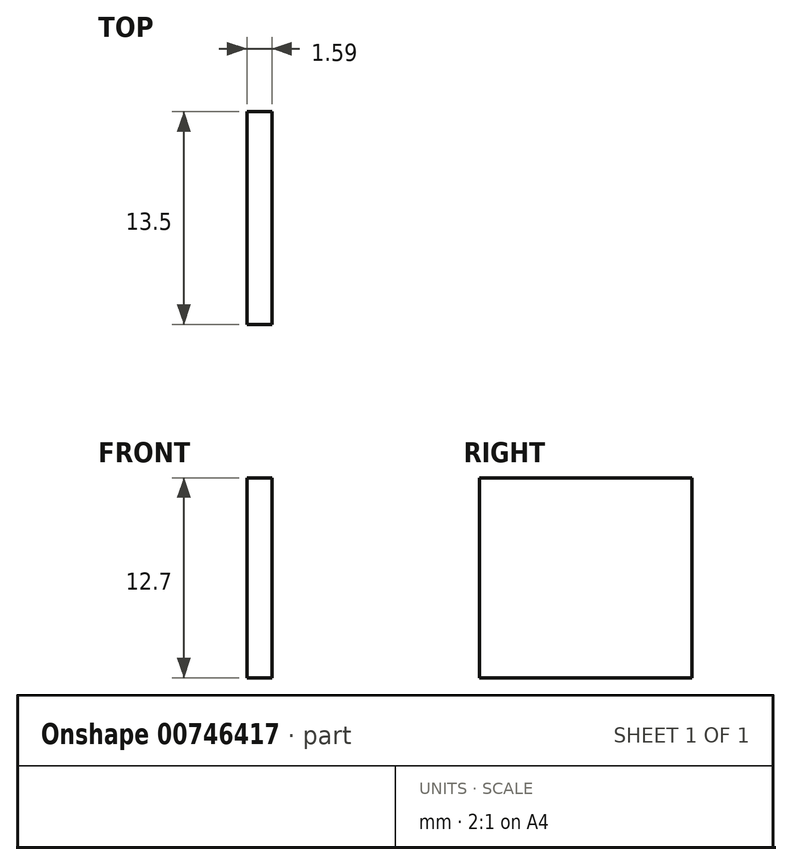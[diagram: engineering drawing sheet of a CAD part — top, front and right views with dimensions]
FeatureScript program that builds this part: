
annotation { "Feature Type Name" : "Feature", "Feature Type Description" : "" }
export const myFeature = defineFeature(function(context is Context, id is Id, definition is map)
    precondition{}
    {
        {
            var Q0;
            Q0=qCreatedBy(makeId("Right.planeOp"),FACE);
            var sketch = newSketch(context, id + "F0", { "sketchPlane" : qUnion([Q0])});
            skLineSegment(sketch, "E0.bottom", {"start": v(-6.75, 6.35) * mm, "end": v(6.75, 6.35) * mm});
            skLineSegment(sketch, "E0.top", {"start": v(-6.75, -6.35) * mm, "end": v(6.75, -6.35) * mm});
            skLineSegment(sketch, "E0.left", {"start": v(-6.75, 6.35) * mm, "end": v(-6.75, -6.35) * mm});
            skLineSegment(sketch, "E0.right", {"start": v(6.75, 6.35) * mm, "end": v(6.75, -6.35) * mm});
            skPoint(sketch, "E0.middle", {"position": v(0, 0) * mm});
            skSolve(sketch);
        }
        {
            var Q0;
            Q0 = qSketchRegion(id + "F0", true);
            extrude(context, id + "F1", {"entities" : qUnion([Q0]), "depth" : 1.59 * mm, "offsetDistance" : 25.4 * mm});
        }
    });
